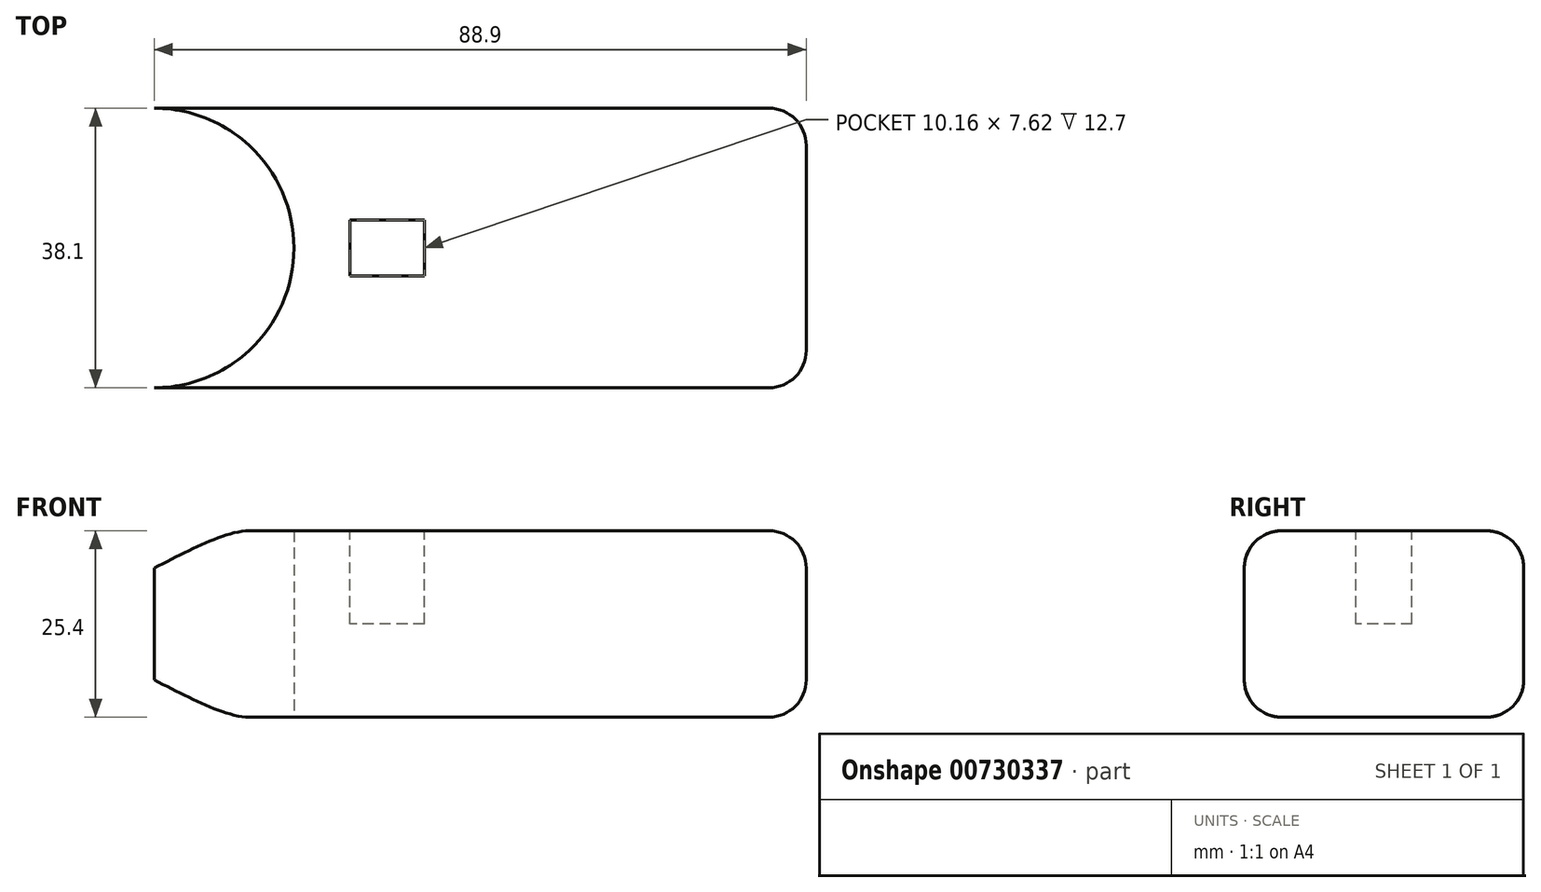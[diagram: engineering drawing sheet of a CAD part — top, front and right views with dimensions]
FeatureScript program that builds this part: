
annotation { "Feature Type Name" : "Feature", "Feature Type Description" : "" }
export const myFeature = defineFeature(function(context is Context, id is Id, definition is map)
    precondition{}
    {
        {
            var Q0;
            Q0=qCreatedBy(makeId("Top.planeOp"),FACE);
            var sketch = newSketch(context, id + "F0", { "sketchPlane" : qUnion([Q0])});
            skArc(sketch, "E0", {"start": v(0, -19.05) * mm, "mid": v(19.05, 0) * mm, "end": v(0, 19.05) * mm});
            skLineSegment(sketch, "E1", {"start": v(0, 19.05) * mm, "end": v(88.9, 19.05) * mm});
            skLineSegment(sketch, "E2", {"start": v(0, -19.05) * mm, "end": v(88.9, -19.05) * mm});
            skLineSegment(sketch, "E3", {"start": v(88.9, -19.05) * mm, "end": v(88.9, 19.05) * mm});
            skSolve(sketch);
        }
        {
            var Q0;
            Q0=makeQuery(id+"F0.imprint","IMPRINT",FACE,{"disambiguationData":[TD([[makeQuery(id+"F0.imprint","IMPRINT",EDGE,{"derivedFrom":sQuery(id+"F0.wireOp",EDGE,"E0")}),-1.0]])]});
            extrude(context, id + "F1", {"entities" : qUnion([Q0]), "depth" : 25.4 * mm, "offsetDistance" : 25.4 * mm});
        }
        {
            var Q0;
            Q0=makeQuery(id+"F1.opExtrude","CAP_FACE",FACE,{"disambiguationData":[OSD([sQuery(id+"F0.wireOp",EDGE,"E0"),sQuery(id+"F0.wireOp",EDGE,"E1"),sQuery(id+"F0.wireOp",EDGE,"E2"),sQuery(id+"F0.wireOp",EDGE,"E3")])],"isStart":false});
            var sketch = newSketch(context, id + "F2", { "sketchPlane" : qUnion([Q0])});
            skLineSegment(sketch, "E4", {"start": v(26.67, 3.81) * mm, "end": v(26.67, -3.81) * mm});
            skLineSegment(sketch, "E5", {"start": v(26.67, -3.81) * mm, "end": v(36.83, -3.81) * mm});
            skLineSegment(sketch, "E6", {"start": v(36.83, -3.81) * mm, "end": v(36.83, 3.8) * mm});
            skLineSegment(sketch, "E7", {"start": v(36.83, 3.81) * mm, "end": v(26.67, 3.81) * mm});
            skSolve(sketch);
        }
        {
            var Q0;
            Q0=makeQuery(id+"F2.imprint","IMPRINT",FACE,{"disambiguationData":[TD([[makeQuery(id+"F2.imprint","IMPRINT",EDGE,{"derivedFrom":sQuery(id+"F2.wireOp",EDGE,"E4")}),1.0]])]});
            extrude(context, id + "F3", {"entities" : qUnion([Q0]), "operationType" : NewBodyOperationType.REMOVE, "oppositeDirection" : true, "depth" : 12.7 * mm, "offsetDistance" : 25.4 * mm});
        }
        {
            var Q0;
            Q0=makeQuery(id+"F1.opExtrude","CAP_EDGE",EDGE,{"disambiguationData":[OSD([sQuery(id+"F0.wireOp",EDGE,"E2")])],"isStart":false});
            var Q1;
            Q1=makeQuery(id+"F1.opExtrude","CAP_EDGE",EDGE,{"disambiguationData":[OSD([sQuery(id+"F0.wireOp",EDGE,"E1")])],"isStart":false});
            var Q2;
            Q2=makeQuery(id+"F1.opExtrude","CAP_EDGE",EDGE,{"disambiguationData":[OSD([sQuery(id+"F0.wireOp",EDGE,"E1")])],"isStart":true});
            var Q3;
            Q3=makeQuery(id+"F1.opExtrude","CAP_EDGE",EDGE,{"disambiguationData":[OSD([sQuery(id+"F0.wireOp",EDGE,"E2")])],"isStart":true});
            var Q4;
            Q4=makeQuery(id+"F1.opExtrude","SWEPT_FACE",FACE,{"disambiguationData":[OSD([sQuery(id+"F0.wireOp",EDGE,"E3")])]});
            fillet(context, id + "F4", {"entities" : qUnion([Q0, Q1, Q2, Q3, Q4]), "radius" : 5.08 * mm, "tangentPropagation" : true, "allowEdgeOverflow" : false});
        }
    });
